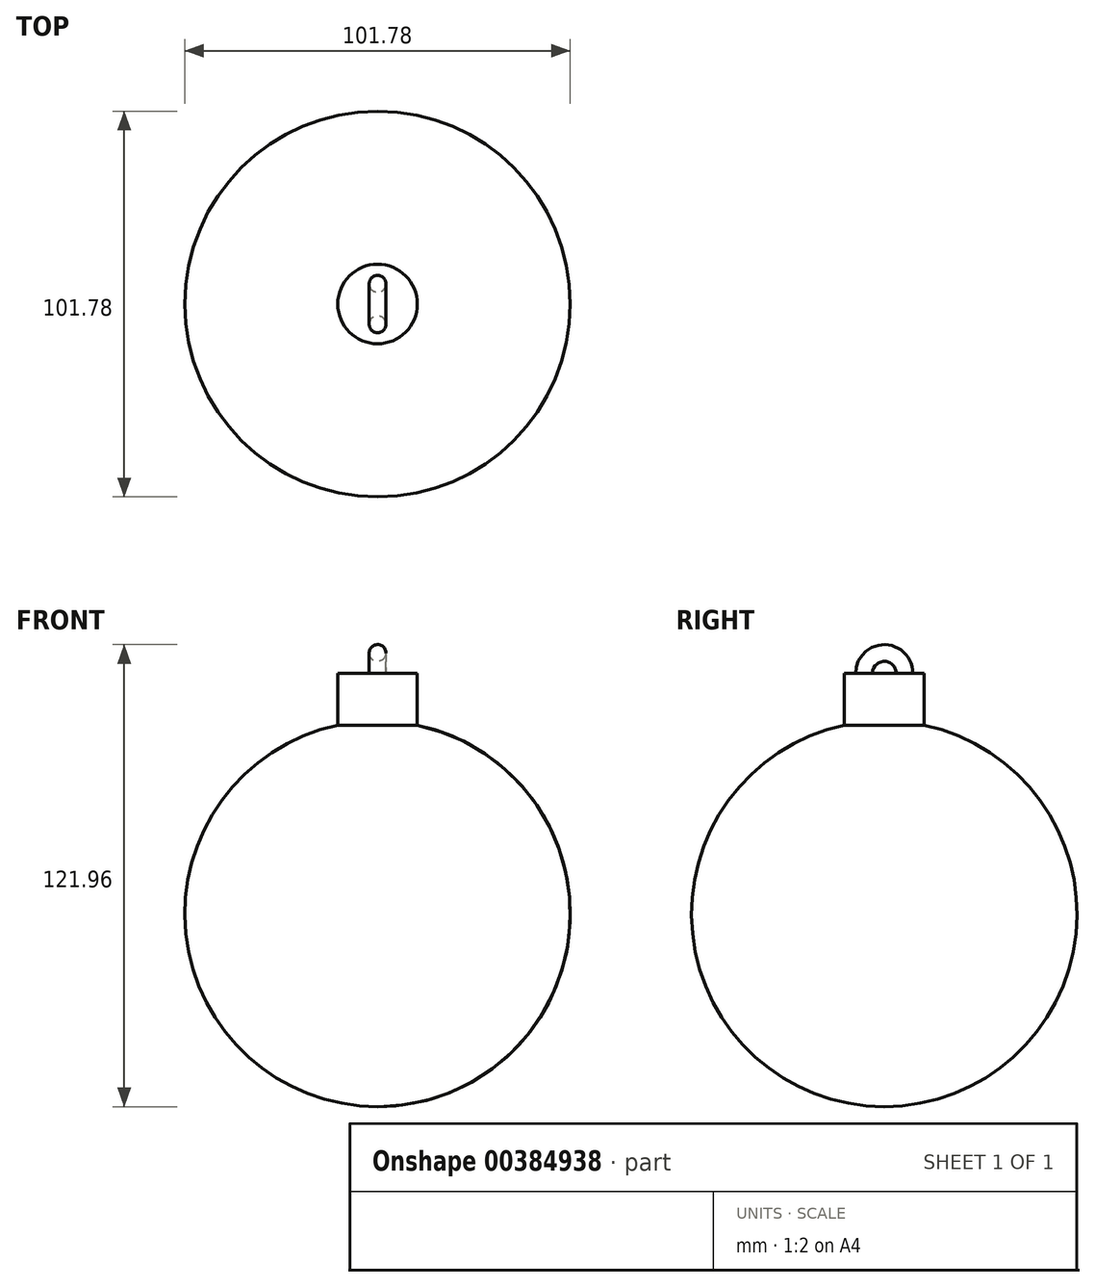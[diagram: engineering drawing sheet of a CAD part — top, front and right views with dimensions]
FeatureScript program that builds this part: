
annotation { "Feature Type Name" : "Feature", "Feature Type Description" : "" }
export const myFeature = defineFeature(function(context is Context, id is Id, definition is map)
    precondition{}
    {
        {
            var Q0;
            Q0=qCreatedBy(makeId("Front.planeOp"),FACE);
            var sketch = newSketch(context, id + "F0", { "sketchPlane" : qUnion([Q0])});
            skArc(sketch, "E0", {"start": v(0, 50.89) * mm, "mid": v(-50.89, 0) * mm, "end": v(0, -50.89) * mm});
            skLineSegment(sketch, "E1", {"start": v(0, 50.89) * mm, "end": v(0, -50.89) * mm});
            skSolve(sketch);
        }
        {
            var Q0;
            Q0=makeQuery(id+"F0.imprint","IMPRINT",FACE,{"disambiguationData":[TD([[makeQuery(id+"F0.imprint","IMPRINT",EDGE,{"derivedFrom":sQuery(id+"F0.wireOp",EDGE,"E0")}),1.0]])]});
            var Q1;
            Q1=sQuery(id+"F0.wireOp",EDGE,"E1");
            revolve(context, id + "F1", {"entities" : qUnion([Q0]), "axis" : qUnion([Q1]), "revolveType" : RevolveType.FULL});
        }
        {
            var Q0;
            Q0=qCreatedBy(makeId("Top.planeOp"),FACE);
            var sketch = newSketch(context, id + "F2", { "sketchPlane" : qUnion([Q0])});
            skCircle(sketch, "E2", {"center": v(0, 0) * mm, "radius": 10.5 * mm});
            skSolve(sketch);
        }
        {
            var Q0;
            Q0 = qSketchRegion(id + "F2", true);
            extrude(context, id + "F3", {"entities" : qUnion([Q0]), "operationType" : NewBodyOperationType.ADD, "depth" : 63.5 * mm});
        }
        {
            var Q0;
            Q0=makeQuery(id+"F3.opExtrude","CAP_FACE",FACE,{"disambiguationData":[OSD([sQuery(id+"F2.wireOp",EDGE,"E2")])],"isStart":false});
            var sketch = newSketch(context, id + "F4", { "sketchPlane" : qUnion([Q0])});
            skLineSegment(sketch, "E3", {"start": v(-6.46, 0) * mm, "end": v(6.23, 0) * mm});
            skCircle(sketch, "E4", {"center": v(0, 5.35) * mm, "radius": 2.22 * mm});
            skSolve(sketch);
        }
        {
            var Q0;
            Q0 = qSketchRegion(id + "F4", true);
            var Q1;
            Q1=sQuery(id+"F4.wireOp",EDGE,"E3");
            revolve(context, id + "F5", {"operationType" : NewBodyOperationType.ADD, "entities" : qUnion([Q0]), "axis" : qUnion([Q1]), "revolveType" : RevolveType.FULL});
        }
    });
